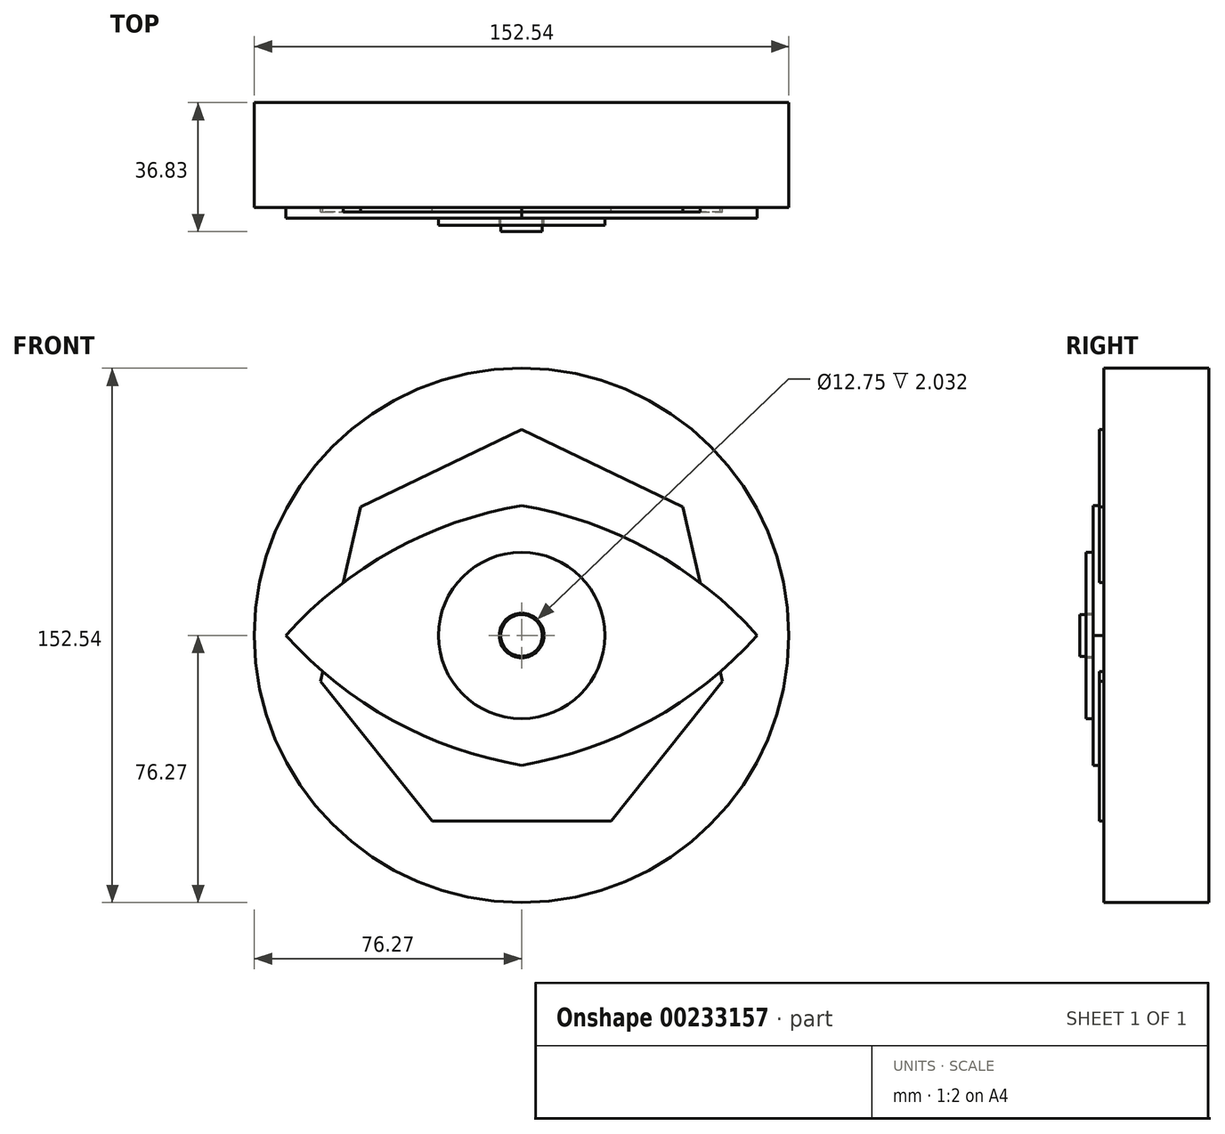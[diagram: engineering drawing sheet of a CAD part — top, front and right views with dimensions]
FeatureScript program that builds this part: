
annotation { "Feature Type Name" : "Feature", "Feature Type Description" : "" }
export const myFeature = defineFeature(function(context is Context, id is Id, definition is map)
    precondition{}
    {
        {
            var Q0;
            Q0=qCreatedBy(makeId("Front.planeOp"),FACE);
            var sketch = newSketch(context, id + "F0", { "sketchPlane" : qUnion([Q0])});
            skCircle(sketch, "E0", {"center": v(0, 0) * mm, "radius": 76.27 * mm});
            skSolve(sketch);
        }
        {
            var Q0;
            Q0 = qSketchRegion(id + "F0", true);
            extrude(context, id + "F1", {"entities" : qUnion([Q0]), "depth" : 29.97 * mm});
        }
        {
            var Q0;
            Q0=qCreatedBy(makeId("Front.planeOp"),FACE);
            var sketch = newSketch(context, id + "F2", { "sketchPlane" : qUnion([Q0])});
            skArc(sketch, "E1", {"start": v(0, 37.04) * mm, "mid": v(-36.78, 24.24) * mm, "end": v(-67.25, 0) * mm});
            skArc(sketch, "E2.MirrorCS", {"start": v(0, -37.04) * mm, "mid": v(-36.78, -24.24) * mm, "end": v(-67.25, 0) * mm});
            skArc(sketch, "E3.MirrorCS", {"start": v(0, 37.04) * mm, "mid": v(36.78, 24.24) * mm, "end": v(67.25, 0) * mm});
            skArc(sketch, "E4.MirrorCS", {"start": v(0, -37.04) * mm, "mid": v(36.78, -24.24) * mm, "end": v(67.25, 0) * mm});
            skSolve(sketch);
        }
        {
            var Q0;
            Q0 = qSketchRegion(id + "F2", true);
            extrude(context, id + "F3", {"entities" : qUnion([Q0]), "operationType" : NewBodyOperationType.ADD, "depth" : 33.02 * mm});
        }
        {
            var Q0;
            Q0=qCreatedBy(makeId("Front.planeOp"),FACE);
            var sketch = newSketch(context, id + "F4", { "sketchPlane" : qUnion([Q0])});
            skCircle(sketch, "E5.cCircle", {"center": v(0, 0) * mm, "radius": 53 * mm, "construction": true});
            skLineSegment(sketch, "E5.0", {"start": v(25.52, -53) * mm, "end": v(-25.52, -53) * mm});
            skLineSegment(sketch, "E5.1", {"start": v(-25.52, -53) * mm, "end": v(-57.34, -13.09) * mm});
            skLineSegment(sketch, "E5.2", {"start": v(-57.34, -13.09) * mm, "end": v(-45.98, 36.67) * mm});
            skLineSegment(sketch, "E5.3", {"start": v(-45.98, 36.67) * mm, "end": v(0, 58.82) * mm});
            skLineSegment(sketch, "E5.4", {"start": v(0, 58.82) * mm, "end": v(45.98, 36.67) * mm});
            skLineSegment(sketch, "E5.5", {"start": v(45.98, 36.67) * mm, "end": v(57.34, -13.09) * mm});
            skLineSegment(sketch, "E5.6", {"start": v(57.34, -13.09) * mm, "end": v(25.52, -53) * mm});
            skPoint(sketch, "E5.0.midPoint", {"position": v(0, -53) * mm});
            skSolve(sketch);
        }
        {
            var Q0;
            Q0 = qSketchRegion(id + "F4", true);
            extrude(context, id + "F5", {"entities" : qUnion([Q0]), "operationType" : NewBodyOperationType.ADD, "depth" : 31.24 * mm});
        }
        {
            var Q0;
            Q0=qCreatedBy(makeId("Front.planeOp"),FACE);
            var sketch = newSketch(context, id + "F6", { "sketchPlane" : qUnion([Q0])});
            skCircle(sketch, "E6", {"center": v(0, 0) * mm, "radius": 23.72 * mm});
            skCircle(sketch, "E7", {"center": v(0, 0) * mm, "radius": 6.37 * mm});
            skSolve(sketch);
        }
        {
            var Q0;
            Q0 = qSketchRegion(id + "F6", true);
            extrude(context, id + "F7", {"entities" : qUnion([Q0]), "operationType" : NewBodyOperationType.ADD, "depth" : 35.05 * mm});
        }
        {
            var Q0;
            Q0=qCreatedBy(makeId("Front.planeOp"),FACE);
            var sketch = newSketch(context, id + "F8", { "sketchPlane" : qUnion([Q0])});
            skCircle(sketch, "E8", {"center": v(0, 0) * mm, "radius": 5.93 * mm});
            skSolve(sketch);
        }
        {
            var Q0;
            Q0 = qSketchRegion(id + "F8", true);
            extrude(context, id + "F9", {"entities" : qUnion([Q0]), "operationType" : NewBodyOperationType.ADD, "depth" : 36.83 * mm});
        }
    });
